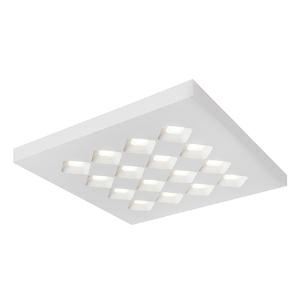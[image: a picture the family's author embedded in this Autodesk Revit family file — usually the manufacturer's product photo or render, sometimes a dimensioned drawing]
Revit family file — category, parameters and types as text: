
# Revit family: 3f_filippi_-_3f_diagon_p_soft_ugr_3f_filippi_-_12130_-_3f_diagon_p_25w-840_soft_ugr_596x596
name_source: partatom
category: Lighting Fixtures
units: mm (PartAtom-declared; Revit-internal decimal feet)

## family parameters
Cut with Voids When Loaded = No
Host = Face
Light Source = No
Part Type = Normal
Room Calculation Point = No
Round Connector Dimension = Use Diameter
Shared = No

## types (1)
- 3F Filippi - 3F Dìagon P Soft UGR (1 x LED, 3679 lm, 28 W, 4000 K)
    Apparent Load = 28 VA
    Approval mark = CE
    CIE Flux Codes = 59 92 100 100 100
    Color Rendering = 80
    Color Temperature = 4000 K
    Control Gear = Electronic ballast
    Default Elevation = 1800 mm
    Description = ILLUMINOTECHNICAL
Luminous efficiency 100% (DLOR 100%, ULOR 0%).
Initial luminous flux of the luminaire 3679 lm.
Direct symmetric distribution.
Installation Interdistance Transv.D = 1.23 x hu - Long.D = 1.23 x hu.
Average luminance <3000 cd/m² for radial angles >65°.
Tabular UGR (CIE 117 - 4H-8H; S=0.25H; 70/50/20): RUG 18.7 - 18.7.
Beam angle: 102° - 101°.
Luminous efficacy 131 lm/W.
Lifetime (L95/B10): 30000 h. (tq+25°C)
Lifetime (L90/B10): 50000 h. (tq+25°C)
Lifetime (L80/B10): 80000 h. (tq+25°C)
Lifetime (L75/B10): 100000 h. (tq+25°C)
Sudden decreased luminous flux after 50000 hours: 0% (C0).
Photobiological safety in compliance with IEC/TR 62778: RG0 risk exempt, (IEC 62471).
In compliance with IEC/EN 62722-2-1 - IEC/EN 62717 standards.

SOURCE
Squared LED module 25W/840.
Energy efficiency class (UE 2019/2020 - UE 2019/2015): C.
CIE 13.3 Colour rendering index: CRI >80 (R9 <50%).
IES TM-30 Fidelity Index: Rf = 84 Rg = 95.
CCT nominal colour temperature 4000 K.
Colour initial tolerance (MacAdam): SDCM 3.

MECHANICAL
White painted frame.
Height only 40 mm.
Housing in hot-galvanised steel, painted in white polyester.
Honeycombed diagonal screen in white anti-glare polycarbonate.
Opal methacrylate (PMMA) rhomboid lenses with differentiated, engraved and prismatic surfaces for diffused, soft lighting and excellent visual comfort.
Luminaire with limited surface temperature. - D - (EN 60598-2-24)
Dimensions: 596x596 mm, height 40 mm. Weight 6.27 kg.
IP40 protection degree.
Mechanical strength to impacts IK06 (1 joule).
Glow-wire test resistance 650°C.

ELECTRICAL
Halogen Free electronic wiring 230V-50/60Hz, power factor 0.95, THD <25%, constant output current, class I, 1 driver.
Power of the luminaire 28 W.
ENEC - CE.
SAFE FLICKER: PstLM=<1 and SVM=<0.4 (IEC TR 61547-1 and IEC TR 63158), to ensure a more comfortable and safe light.
Luminaire compliant with EN 60598-2-22 for power supply from a centralised emergency system CPSS (Central Power Supply System), not incorporated in the luminaire - high risk areas excluded. The default power and flux are 100% in AC and 100% in DC.
Ambient temperature from 0°C to +25°C.
Temperature class T6 max 85°C.
Quick connection.
Relative humidity UR: <85%.

INSTALLATION
Ceiling.

APPLICATIONS
Environments: staterooms, with VDTs, offices.
Environments with exacting visual tasks, where diffused soft light for optimum visual comfort is required.

WARNING
Luminaire designed for disposal/recycling at end-of-life.
Replaceable (LED only) light source by a professional. Replaceable control gear by a professional.
    Height = 40 mm  [stored 0.131234 ft]
    Lamp = 1 x LED
    Lamp Light Flux = 3679 lm
    Lamp Power = 28 W
    Lamp count = 1
    Length = 596 mm
    Lifetime = 50000 h
    Luminous efficacy = 131 lm/W
    Manufacturer = 3F Filippi
    ModVariant = No
    Model = 3F Filippi - 12130 - 3F Diagon P 25W-840 SOFT UGR 596x596
    Mounting Place = Ceiling
    Mounting Type = Surface mounted
    Number of Poles = 1
    OnlyDefault = Yes
    Power Factor = 1
    Product Name = 3F Filippi - 3F Dìagon P Soft UGR
    Product group = ceiling mounted luminaire
    ProductGroupID = 3
    Protection Class = Protection class I
    Protection Degree = IP 40
    RLX_Detail_Level = 1
    RLX_Emergency_Light_Flux = 0 lm
    RLX_Emergency_Type = 0
    RLX_Emergency_Type_DB = No
    RlxData = <blob elided: 94985 chars, md5=0931c0d4>
    Socket = socket
    Standby Power = 0 W
    System Light Flux = 3679 lm
    System Power = 28 W
    Type Comments = Product without accessories
    Type Image = 3ffilippi_3f_diagon_p_soft_ugr.jpg
    URL = http://relux.com
    VarID = ---
    Voltage = 0 V
    Weight = 0.00 kg
    Width = 596 mm

note: [stored X ft] marks values corroborated as IEEE doubles in the binary element streams (Revit-internal decimal feet)

## geometry (parser evidence)
native form markers: Blend x4, Sweep x9
no freeform markers — native parametric forms only
